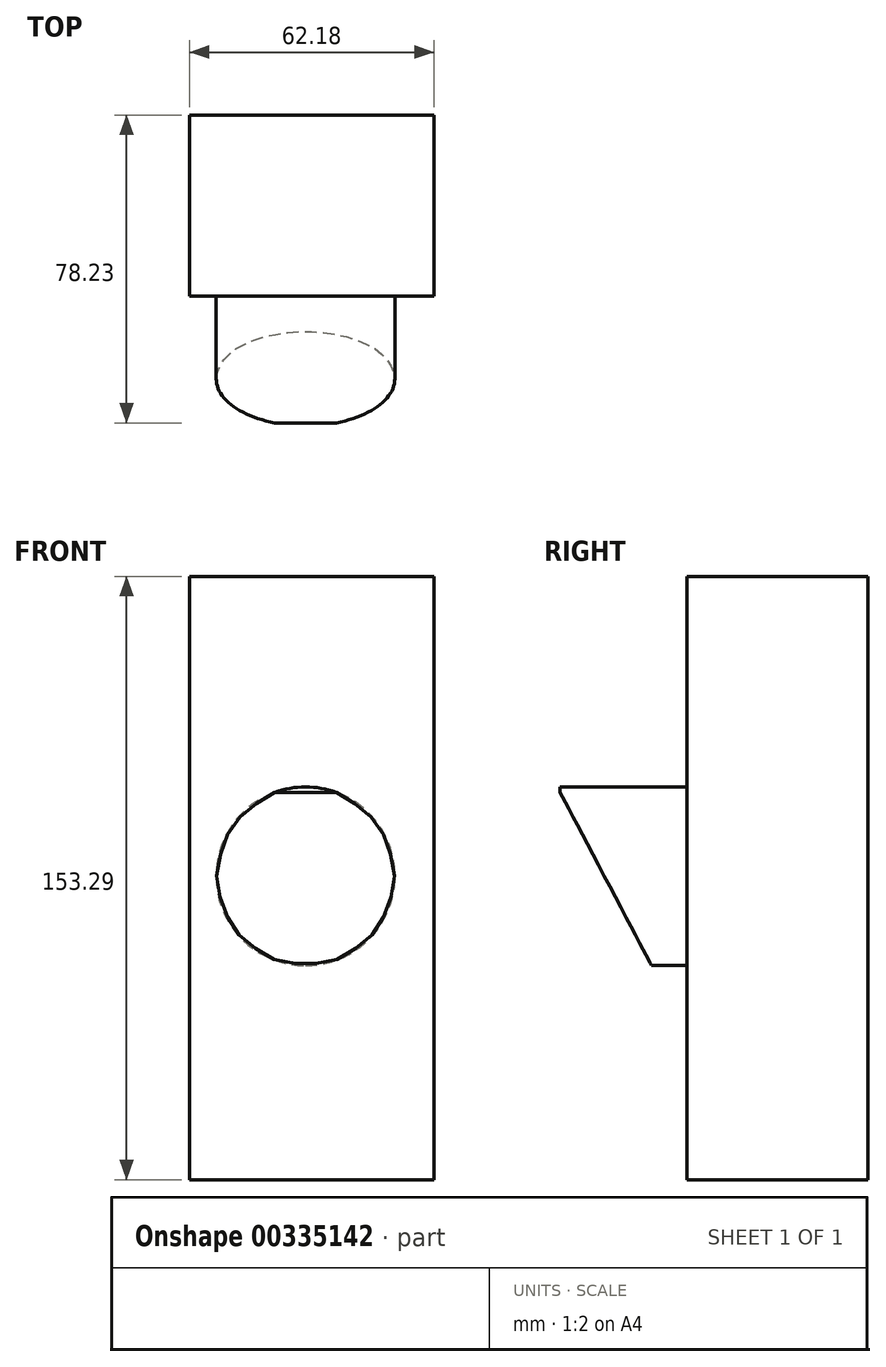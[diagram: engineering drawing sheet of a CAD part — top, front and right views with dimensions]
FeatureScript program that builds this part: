
annotation { "Feature Type Name" : "Feature", "Feature Type Description" : "" }
export const myFeature = defineFeature(function(context is Context, id is Id, definition is map)
    precondition{}
    {
        {
            var Q0;
            Q0=qCreatedBy(makeId("Front.planeOp"),FACE);
            var sketch = newSketch(context, id + "F0", { "sketchPlane" : qUnion([Q0])});
            skLineSegment(sketch, "E0.bottom", {"start": v(-29.5, 76.21) * mm, "end": v(32.68, 76.21) * mm});
            skLineSegment(sketch, "E0.top", {"start": v(-29.5, -77.08) * mm, "end": v(32.68, -77.08) * mm});
            skLineSegment(sketch, "E0.left", {"start": v(-29.5, 76.21) * mm, "end": v(-29.5, -77.08) * mm});
            skLineSegment(sketch, "E0.right", {"start": v(32.68, 76.21) * mm, "end": v(32.68, -77.08) * mm});
            skSolve(sketch);
        }
        {
            var Q0;
            Q0=makeQuery(id+"F0.imprint","IMPRINT",FACE,{"disambiguationData":[TD([[makeQuery(id+"F0.imprint","IMPRINT",EDGE,{"derivedFrom":sQuery(id+"F0.wireOp",EDGE,"E0.bottom")}),-1.0]])]});
            extrude(context, id + "F1", {"entities" : qUnion([Q0]), "depth" : 45.97 * mm});
        }
        {
            var Q0;
            Q0=makeQuery(id+"F1.opExtrude","CAP_FACE",FACE,{"disambiguationData":[OSD([sQuery(id+"F0.wireOp",EDGE,"E0.bottom"),sQuery(id+"F0.wireOp",EDGE,"E0.top"),sQuery(id+"F0.wireOp",EDGE,"E0.left"),sQuery(id+"F0.wireOp",EDGE,"E0.right")])],"isStart":false});
            var sketch = newSketch(context, id + "F2", { "sketchPlane" : qUnion([Q0])});
            skCircle(sketch, "E1", {"center": v(0, 0) * mm, "radius": 22.7 * mm});
            skSolve(sketch);
        }
        {
            var Q0;
            Q0=makeQuery(id+"F2.imprint","IMPRINT",FACE,{"disambiguationData":[TD([[makeQuery(id+"F2.imprint","IMPRINT",EDGE,{"derivedFrom":sQuery(id+"F2.wireOp",EDGE,"E1")}),1.0]])]});
            var Q1;
            Q1=sQuery(id+"F2.wireOp",EDGE,"E1");
            extrude(context, id + "F3", {"entities" : qUnion([Q0]), "operationType" : NewBodyOperationType.ADD, "surfaceEntities" : qUnion([Q1]), "depth" : 32.26 * mm});
        }
        {
            var Q0;
            Q0=qCreatedBy(makeId("Right.planeOp"),FACE);
            var sketch = newSketch(context, id + "F4", { "sketchPlane" : qUnion([Q0])});
            skLineSegment(sketch, "E2", {"start": v(-78.85, 22.49) * mm, "end": v(-53.61, -25.31) * mm});
            skLineSegment(sketch, "E3", {"start": v(-53.61, -25.31) * mm, "end": v(-78.63, -25.31) * mm});
            skLineSegment(sketch, "E4", {"start": v(-78.63, -25.31) * mm, "end": v(-78.85, 22.49) * mm});
            skSolve(sketch);
        }
        {
            var Q0;
            Q0 = qSketchRegion(id + "F4", true);
            extrude(context, id + "F5", {"entities" : qUnion([Q0]), "operationType" : NewBodyOperationType.REMOVE, "endBound" : BoundingType.SYMMETRIC, "oppositeDirection" : true, "depth" : 48.77 * mm});
        }
    });
